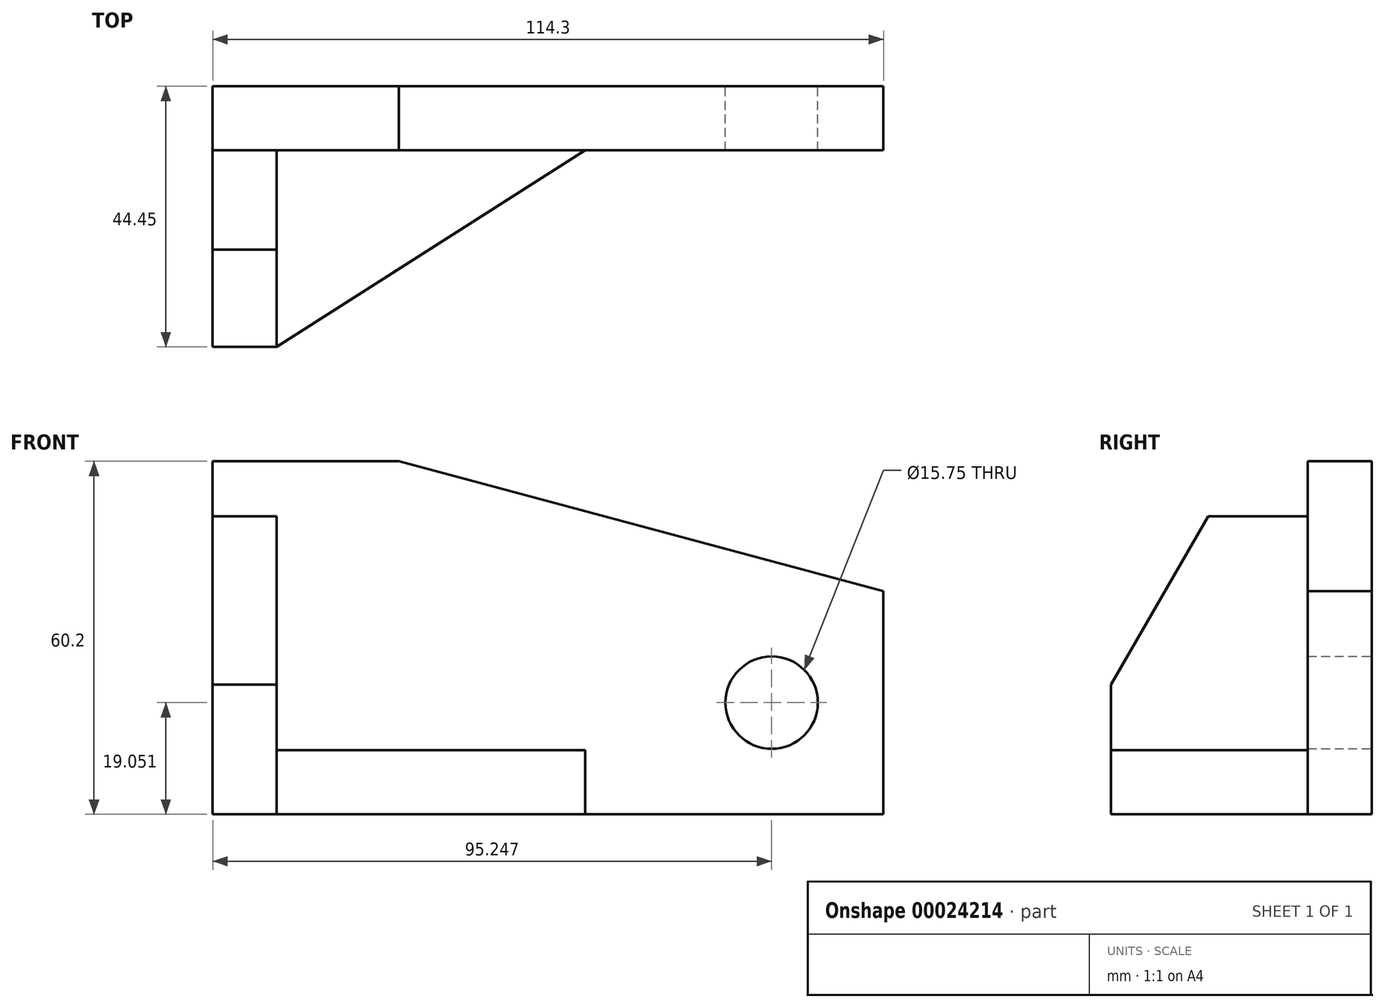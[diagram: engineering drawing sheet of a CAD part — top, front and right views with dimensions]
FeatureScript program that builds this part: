
annotation { "Feature Type Name" : "Feature", "Feature Type Description" : "" }
export const myFeature = defineFeature(function(context is Context, id is Id, definition is map)
    precondition{}
    {
        {
            var Q0;
            Q0=qCreatedBy(makeId("Front.planeOp"),FACE);
            var sketch = newSketch(context, id + "F0", { "sketchPlane" : qUnion([Q0])});
            skLineSegment(sketch, "E0.bottom", {"start": v(-49.3, 32.8) * mm, "end": v(65, 32.8) * mm});
            skLineSegment(sketch, "E0.top", {"start": v(-49.3, -27.39) * mm, "end": v(65, -27.39) * mm});
            skLineSegment(sketch, "E0.left", {"start": v(-49.3, 32.8) * mm, "end": v(-49.3, -27.39) * mm});
            skLineSegment(sketch, "E0.right", {"start": v(65, 32.8) * mm, "end": v(65, -27.39) * mm});
            skLineSegment(sketch, "E1", {"start": v(-17.55, 32.8) * mm, "end": v(65, 10.69) * mm});
            skCircle(sketch, "E2", {"center": v(45.95, -8.34) * mm, "radius": 7.87 * mm});
            skSolve(sketch);
        }
        {
            var Q0;
            {var subQ2=sQuery(id+"F0.wireOp",EDGE,"E0.top");Q0=makeQuery(id+"F0.imprint","IMPRINT",FACE,{"disambiguationData":[TD([[makeQuery(id+"F0.imprint","IMPRINT",EDGE,{"derivedFrom":subQ2}),1.0]])]});}
            extrude(context, id + "F1", {"entities" : qUnion([Q0]), "depth" : 10.92 * mm});
        }
        {
            var Q0;
            Q0=makeQuery(id+"F1.opExtrude","SWEPT_FACE",FACE,{"disambiguationData":[OSD([sQuery(id+"F0.wireOp",EDGE,"E0.left")])]});
            var sketch = newSketch(context, id + "F2", { "sketchPlane" : qUnion([Q0])});
            skLineSegment(sketch, "E3.bottom", {"start": v(10.92, -27.39) * mm, "end": v(44.45, -27.39) * mm});
            skLineSegment(sketch, "E3.top", {"start": v(10.92, 23.41) * mm, "end": v(44.45, 23.41) * mm});
            skLineSegment(sketch, "E3.left", {"start": v(10.92, -27.39) * mm, "end": v(10.92, 23.41) * mm});
            skLineSegment(sketch, "E3.right", {"start": v(44.45, -27.39) * mm, "end": v(44.45, 23.41) * mm});
            skLineSegment(sketch, "E4", {"start": v(27.88, 23.41) * mm, "end": v(44.45, -5.3) * mm});
            skLineSegment(sketch, "E5", {"start": v(44.45, -5.3) * mm, "end": v(19.63, 37.7) * mm, "construction": true});
            skSolve(sketch);
        }
        {
            var Q0;
            {var subQ2=sQuery(id+"F2.wireOp",EDGE,"E3.bottom");Q0=makeQuery(id+"F2.imprint","IMPRINT",FACE,{"disambiguationData":[TD([[makeQuery(id+"F2.imprint","IMPRINT",EDGE,{"derivedFrom":subQ2}),1.0]])]});}
            extrude(context, id + "F3", {"entities" : qUnion([Q0]), "oppositeDirection" : true, "depth" : 10.92 * mm});
        }
        {
            var Q0;
            Q0=makeQuery(id+"F3.opExtrude","SWEPT_FACE",FACE,{"disambiguationData":[OSD([sQuery(id+"F2.wireOp",EDGE,"E3.bottom")])]});
            var sketch = newSketch(context, id + "F4", { "sketchPlane" : qUnion([Q0])});
            skLineSegment(sketch, "E6.bottom", {"start": v(-38.38, 10.92) * mm, "end": v(14.2, 10.92) * mm});
            skLineSegment(sketch, "E6.top", {"start": v(-38.38, 44.45) * mm, "end": v(14.2, 44.45) * mm});
            skLineSegment(sketch, "E6.left", {"start": v(-38.38, 10.92) * mm, "end": v(-38.38, 44.45) * mm});
            skLineSegment(sketch, "E6.right", {"start": v(14.2, 10.92) * mm, "end": v(14.2, 44.45) * mm});
            skLineSegment(sketch, "E7", {"start": v(-38.38, 44.45) * mm, "end": v(14.2, 10.92) * mm});
            skSolve(sketch);
        }
        {
            var Q0;
            Q0=makeQuery(id+"F4.imprint","IMPRINT",FACE,{"disambiguationData":[TD([[makeQuery(id+"F4.imprint","IMPRINT",EDGE,{"derivedFrom":sQuery(id+"F4.wireOp",EDGE,"E6.bottom")}),1.0]])]});
            extrude(context, id + "F5", {"entities" : qUnion([Q0]), "oppositeDirection" : true, "depth" : 10.92 * mm});
        }
    });
